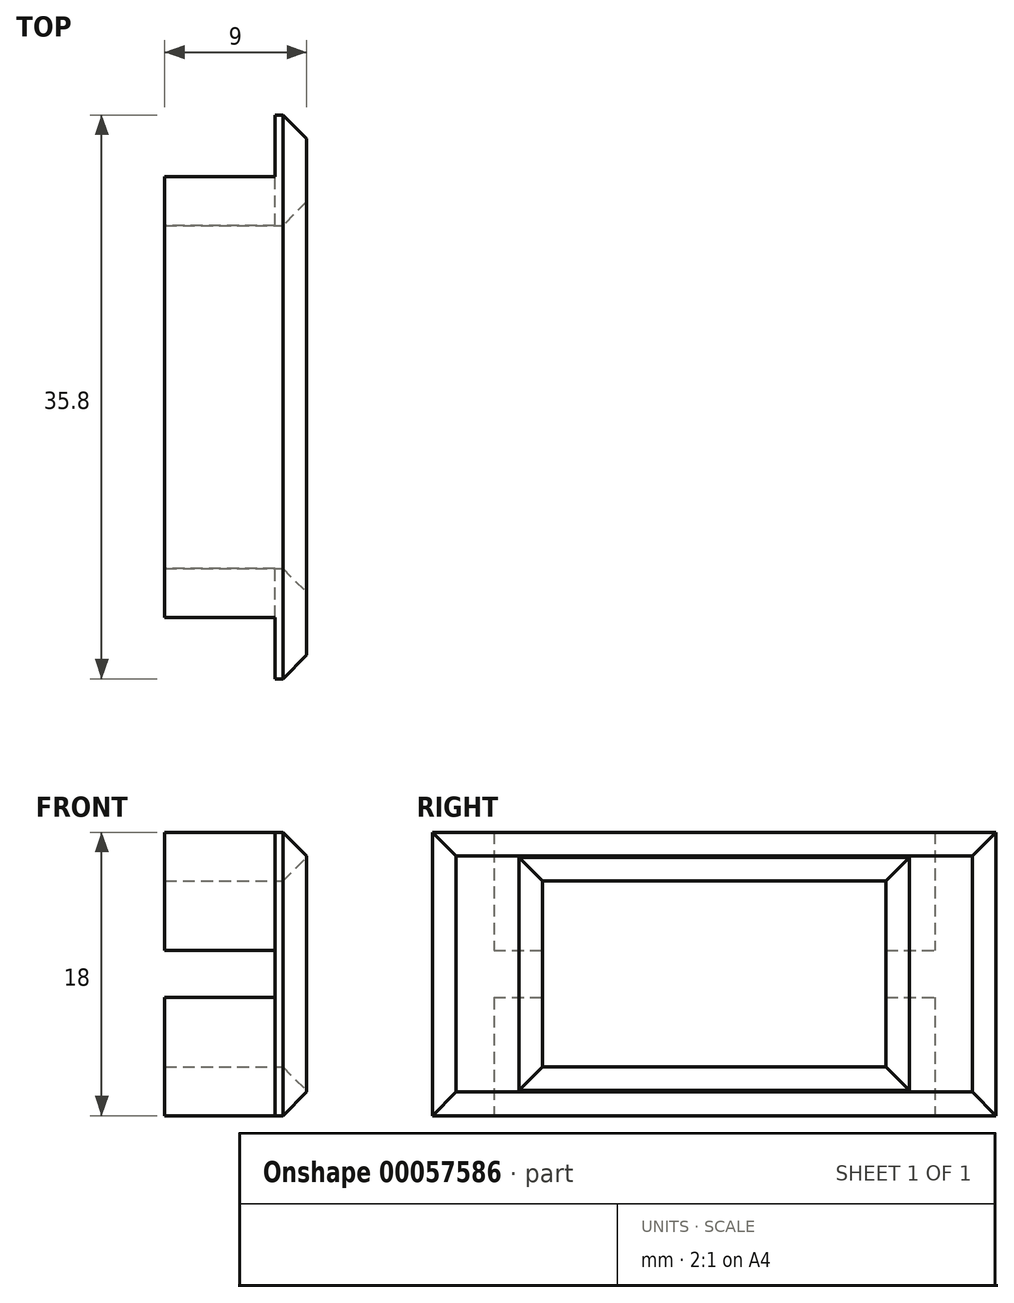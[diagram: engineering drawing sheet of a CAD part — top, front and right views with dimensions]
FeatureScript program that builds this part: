
annotation { "Feature Type Name" : "Feature", "Feature Type Description" : "" }
export const myFeature = defineFeature(function(context is Context, id is Id, definition is map)
    precondition{}
    {
        {
            var Q0;
            Q0=qCreatedBy(makeId("Right.planeOp"),FACE);
            var sketch = newSketch(context, id + "F0", { "sketchPlane" : qUnion([Q0])});
            skLineSegment(sketch, "E0.rect.bottom", {"start": v(10.9, 5.9) * mm, "end": v(-10.9, 5.9) * mm});
            skLineSegment(sketch, "E0.rect.top", {"start": v(10.9, -5.9) * mm, "end": v(-10.9, -5.9) * mm});
            skLineSegment(sketch, "E0.rect.left", {"start": v(10.9, 5.9) * mm, "end": v(10.9, -5.9) * mm});
            skLineSegment(sketch, "E0.rect.right", {"start": v(-10.9, 5.9) * mm, "end": v(-10.9, -5.9) * mm});
            skPoint(sketch, "E0.rect.middle", {"position": v(0, 0) * mm});
            skLineSegment(sketch, "E1.rect.bottom", {"start": v(14, 9) * mm, "end": v(-14, 9) * mm});
            skLineSegment(sketch, "E1.rect.top", {"start": v(14, -9) * mm, "end": v(-14, -9) * mm});
            skLineSegment(sketch, "E1.rect.left", {"start": v(14, 9) * mm, "end": v(14, -9) * mm});
            skLineSegment(sketch, "E1.rect.right", {"start": v(-14, 9) * mm, "end": v(-14, -9) * mm});
            skSolve(sketch);
        }
        {
            var Q0;
            Q0 = qSketchRegion(id + "F0", true);
            extrude(context, id + "F1", {"entities" : qUnion([Q0]), "oppositeDirection" : true, "depth" : 7 * mm});
        }
        {
            var Q0;
            Q0=makeQuery(id+"F1.opExtrude","CAP_FACE",FACE,{"disambiguationData":[OSD([sQuery(id+"F0.wireOp",EDGE,"E0.rect.bottom"),sQuery(id+"F0.wireOp",EDGE,"E0.rect.top"),sQuery(id+"F0.wireOp",EDGE,"E0.rect.left"),sQuery(id+"F0.wireOp",EDGE,"E0.rect.right"),sQuery(id+"F0.wireOp",EDGE,"E1.rect.bottom"),sQuery(id+"F0.wireOp",EDGE,"E1.rect.top"),sQuery(id+"F0.wireOp",EDGE,"E1.rect.left"),sQuery(id+"F0.wireOp",EDGE,"E1.rect.right")])],"isStart":true});
            var sketch = newSketch(context, id + "F2", { "sketchPlane" : qUnion([Q0])});
            skLineSegment(sketch, "E2.0", {"start": v(10.9, 5.9) * mm, "end": v(-10.9, 5.9) * mm});
            skLineSegment(sketch, "E2.1", {"start": v(-10.9, 5.9) * mm, "end": v(-10.9, -5.9) * mm});
            skLineSegment(sketch, "E2.2", {"start": v(10.9, -5.9) * mm, "end": v(-10.9, -5.9) * mm});
            skLineSegment(sketch, "E2.3", {"start": v(10.9, 5.9) * mm, "end": v(10.9, -5.9) * mm});
            skLineSegment(sketch, "E3.rect.bottom", {"start": v(17.9, 9) * mm, "end": v(-17.9, 9) * mm});
            skLineSegment(sketch, "E3.rect.top", {"start": v(17.9, -9) * mm, "end": v(-17.9, -9) * mm});
            skLineSegment(sketch, "E3.rect.left", {"start": v(17.9, 9) * mm, "end": v(17.9, -9) * mm});
            skLineSegment(sketch, "E3.rect.right", {"start": v(-17.9, 9) * mm, "end": v(-17.9, -9) * mm});
            skPoint(sketch, "E3.rect.middle", {"position": v(0, 0) * mm});
            skSolve(sketch);
        }
        {
            var Q0;
            Q0 = qSketchRegion(id + "F2", true);
            extrude(context, id + "F3", {"entities" : qUnion([Q0]), "operationType" : NewBodyOperationType.ADD, "depth" : 2 * mm});
        }
        {
            var Q0;
            Q0=makeQuery(id+"F1.opExtrude","SWEPT_FACE",FACE,{"disambiguationData":[OSD([sQuery(id+"F0.wireOp",EDGE,"E1.rect.left")])]});
            var sketch = newSketch(context, id + "F4", { "sketchPlane" : qUnion([Q0])});
            skLineSegment(sketch, "E4.bottom", {"start": v(7, 1.5) * mm, "end": v(0, 1.5) * mm});
            skLineSegment(sketch, "E4.top", {"start": v(7, -1.5) * mm, "end": v(0, -1.5) * mm});
            skLineSegment(sketch, "E4.left", {"start": v(7, 1.5) * mm, "end": v(7, -1.5) * mm});
            skLineSegment(sketch, "E4.right", {"start": v(0, 1.5) * mm, "end": v(0, -1.5) * mm});
            skSolve(sketch);
        }
        {
            var Q0;
            Q0 = qSketchRegion(id + "F4", true);
            extrude(context, id + "F5", {"entities" : qUnion([Q0]), "operationType" : NewBodyOperationType.REMOVE, "endBound" : BoundingType.THROUGH_ALL, "oppositeDirection" : true, "depth" : 25 * mm});
        }
        {
            var Q0;
            Q0=makeQuery(id+"F3.opExtrude","CAP_FACE",FACE,{"disambiguationData":[OSD([sQuery(id+"F2.wireOp",EDGE,"E2.0"),sQuery(id+"F2.wireOp",EDGE,"E2.1"),sQuery(id+"F2.wireOp",EDGE,"E2.2"),sQuery(id+"F2.wireOp",EDGE,"E2.3"),sQuery(id+"F2.wireOp",EDGE,"E3.rect.bottom"),sQuery(id+"F2.wireOp",EDGE,"E3.rect.top"),sQuery(id+"F2.wireOp",EDGE,"E3.rect.left"),sQuery(id+"F2.wireOp",EDGE,"E3.rect.right")])],"isStart":false});
            chamfer(context, id + "F6", {"entities" : qUnion([Q0]), "width" : 1.5 * mm, "tangentPropagation" : true});
        }
    });
